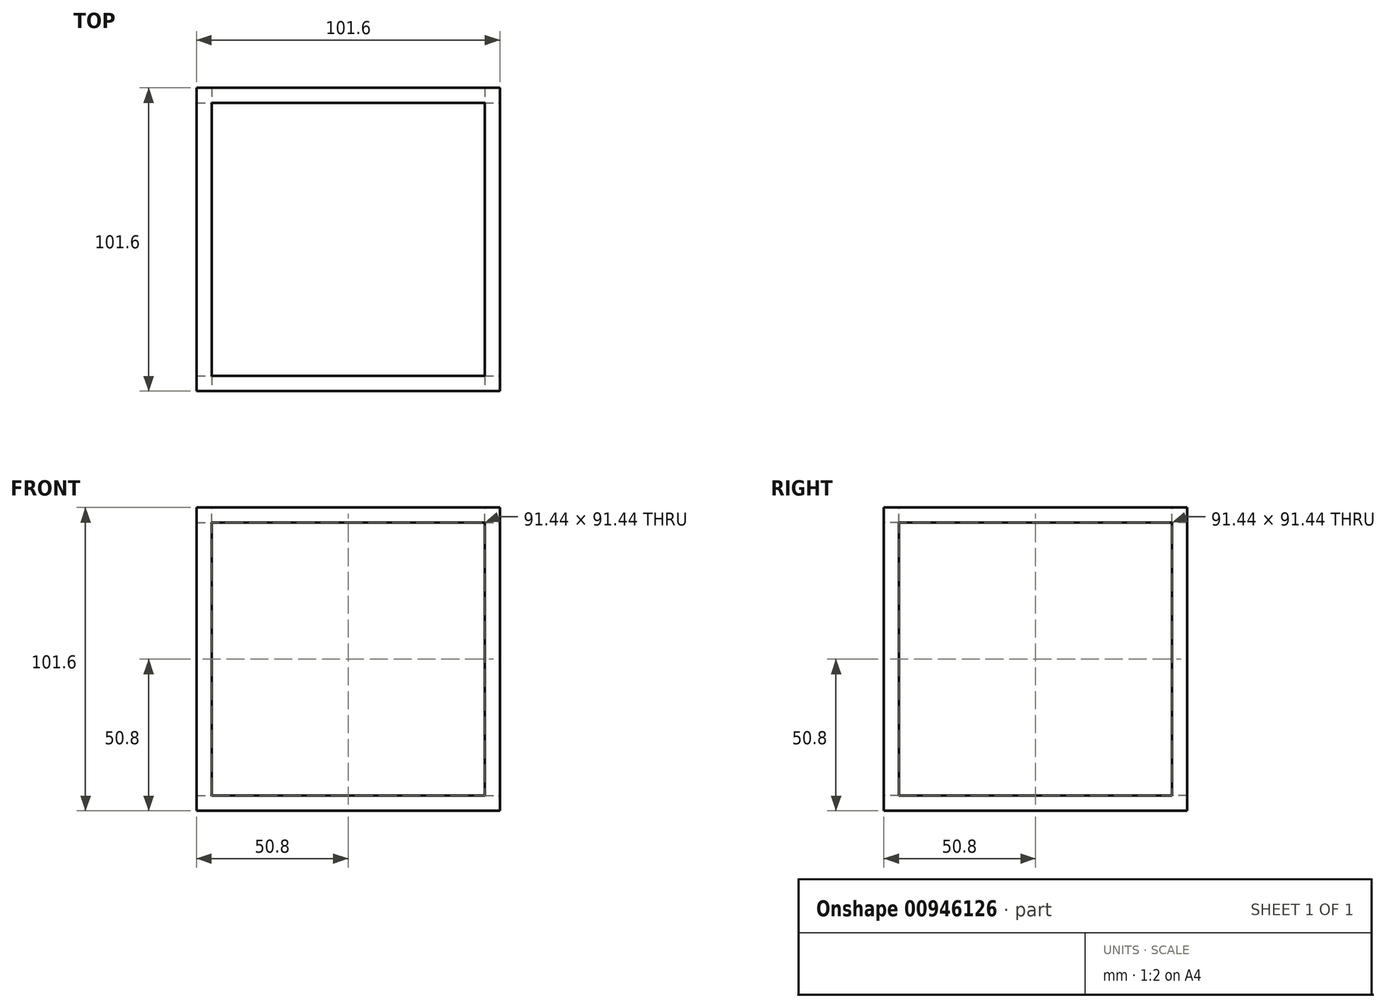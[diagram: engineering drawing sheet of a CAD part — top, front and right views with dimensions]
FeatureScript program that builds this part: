
annotation { "Feature Type Name" : "Feature", "Feature Type Description" : "" }
export const myFeature = defineFeature(function(context is Context, id is Id, definition is map)
    precondition{}
    {
        {
            var Q0;
            Q0=qCreatedBy(makeId("Top.planeOp"),FACE);
            var sketch = newSketch(context, id + "F0", { "sketchPlane" : qUnion([Q0])});
            skLineSegment(sketch, "E0.bottom", {"start": v(50.8, -50.8) * mm, "end": v(-50.8, -50.8) * mm});
            skLineSegment(sketch, "E0.top", {"start": v(50.8, 50.8) * mm, "end": v(-50.8, 50.8) * mm});
            skLineSegment(sketch, "E0.left", {"start": v(50.8, -50.8) * mm, "end": v(50.8, 50.8) * mm});
            skLineSegment(sketch, "E0.right", {"start": v(-50.8, -50.8) * mm, "end": v(-50.8, 50.8) * mm});
            skPoint(sketch, "E0.middle", {"position": v(0, 0) * mm});
            skLineSegment(sketch, "E1.bottom", {"start": v(45.72, -45.72) * mm, "end": v(-45.72, -45.72) * mm});
            skLineSegment(sketch, "E1.top", {"start": v(45.72, 45.72) * mm, "end": v(-45.72, 45.72) * mm});
            skLineSegment(sketch, "E1.left", {"start": v(45.72, -45.72) * mm, "end": v(45.72, 45.72) * mm});
            skLineSegment(sketch, "E1.right", {"start": v(-45.72, -45.72) * mm, "end": v(-45.72, 45.72) * mm});
            skSolve(sketch);
        }
        {
            var Q0;
            Q0=makeQuery(id+"F0.imprint","IMPRINT",FACE,{"disambiguationData":[TD([[makeQuery(id+"F0.imprint","IMPRINT",EDGE,{"derivedFrom":sQuery(id+"F0.wireOp",EDGE,"E0.bottom")}),-1.0]])]});
            var Q1;
            Q1=makeQuery(id+"F0.imprint","IMPRINT",FACE,{"disambiguationData":[TD([[makeQuery(id+"F0.imprint","IMPRINT",EDGE,{"derivedFrom":sQuery(id+"F0.wireOp",EDGE,"E1.bottom")}),-1.0]])]});
            extrude(context, id + "F1", {"entities" : qUnion([Q0, Q1]), "depth" : 101.6 * mm, "offsetDistance" : 25.4 * mm});
        }
        {
            var Q0;
            Q0=makeQuery(id+"F1.opExtrude","SWEPT_FACE",FACE,{"disambiguationData":[OSD([sQuery(id+"F0.wireOp",EDGE,"E0.left")])]});
            var sketch = newSketch(context, id + "F2", { "sketchPlane" : qUnion([Q0])});
            skLineSegment(sketch, "E2", {"start": v(50.8, 0) * mm, "end": v(-50.8, 0) * mm});
            skLineSegment(sketch, "E3.bottom", {"start": v(45.72, 5.08) * mm, "end": v(-45.72, 5.08) * mm});
            skLineSegment(sketch, "E3.top", {"start": v(45.72, 96.52) * mm, "end": v(-45.72, 96.52) * mm});
            skLineSegment(sketch, "E3.left", {"start": v(45.72, 5.08) * mm, "end": v(45.72, 96.52) * mm});
            skLineSegment(sketch, "E3.right", {"start": v(-45.72, 5.08) * mm, "end": v(-45.72, 96.52) * mm});
            skPoint(sketch, "E3.middle", {"position": v(0, 50.8) * mm});
            skSolve(sketch);
        }
        {
            var Q0;
            Q0=makeQuery(id+"F2.imprint","IMPRINT",FACE,{"disambiguationData":[TD([[makeQuery(id+"F2.imprint","IMPRINT",EDGE,{"derivedFrom":sQuery(id+"F2.wireOp",EDGE,"E3.bottom")}),-1.0]])]});
            var Q1;
            Q1=qSketchRegion(id+"F2",true);
            extrude(context, id + "F3", {"entities" : qUnion([Q0, Q1]), "operationType" : NewBodyOperationType.REMOVE, "oppositeDirection" : true, "depth" : 101.6 * mm, "offsetDistance" : 25.4 * mm});
        }
        {
            var Q0;
            Q0=makeQuery(id+"F1.opExtrude","SWEPT_FACE",FACE,{"disambiguationData":[OSD([sQuery(id+"F0.wireOp",EDGE,"E0.bottom")])]});
            var sketch = newSketch(context, id + "F4", { "sketchPlane" : qUnion([Q0])});
            skLineSegment(sketch, "E4.bottom", {"start": v(45.72, 5.08) * mm, "end": v(-45.72, 5.08) * mm});
            skLineSegment(sketch, "E4.top", {"start": v(45.72, 96.52) * mm, "end": v(-45.72, 96.52) * mm});
            skLineSegment(sketch, "E4.left", {"start": v(45.72, 5.08) * mm, "end": v(45.72, 96.52) * mm});
            skLineSegment(sketch, "E4.right", {"start": v(-45.72, 5.08) * mm, "end": v(-45.72, 96.52) * mm});
            skPoint(sketch, "E4.middle", {"position": v(0, 50.8) * mm});
            skSolve(sketch);
        }
        {
            var Q0;
            Q0=makeQuery(id+"F4.imprint","IMPRINT",FACE,{"disambiguationData":[TD([[makeQuery(id+"F4.imprint","IMPRINT",EDGE,{"derivedFrom":sQuery(id+"F4.wireOp",EDGE,"E4.bottom")}),-1.0]])]});
            extrude(context, id + "F5", {"entities" : qUnion([Q0]), "operationType" : NewBodyOperationType.REMOVE, "oppositeDirection" : true, "depth" : 101.6 * mm, "offsetDistance" : 25.4 * mm});
        }
        {
            var Q0;
            Q0=makeQuery(id+"F1.opExtrude","CAP_FACE",FACE,{"disambiguationData":[OSD([sQuery(id+"F0.wireOp",EDGE,"E0.bottom"),sQuery(id+"F0.wireOp",EDGE,"E0.top"),sQuery(id+"F0.wireOp",EDGE,"E0.left"),sQuery(id+"F0.wireOp",EDGE,"E0.right")])],"isStart":false});
            var sketch = newSketch(context, id + "F6", { "sketchPlane" : qUnion([Q0])});
            skLineSegment(sketch, "E5.bottom", {"start": v(45.72, -45.72) * mm, "end": v(-45.72, -45.72) * mm});
            skLineSegment(sketch, "E5.top", {"start": v(45.72, 45.72) * mm, "end": v(-45.72, 45.72) * mm});
            skLineSegment(sketch, "E5.left", {"start": v(45.72, -45.72) * mm, "end": v(45.72, 45.72) * mm});
            skLineSegment(sketch, "E5.right", {"start": v(-45.72, -45.72) * mm, "end": v(-45.72, 45.72) * mm});
            skPoint(sketch, "E5.middle", {"position": v(0, 0) * mm});
            skSolve(sketch);
        }
        {
            var Q0;
            Q0=makeQuery(id+"F6.imprint","IMPRINT",FACE,{"disambiguationData":[TD([[makeQuery(id+"F6.imprint","IMPRINT",EDGE,{"derivedFrom":sQuery(id+"F6.wireOp",EDGE,"E5.bottom")}),-1.0]])]});
            extrude(context, id + "F7", {"entities" : qUnion([Q0]), "operationType" : NewBodyOperationType.REMOVE, "oppositeDirection" : true, "depth" : 25.4 * mm, "offsetDistance" : 25.4 * mm});
        }
    });
